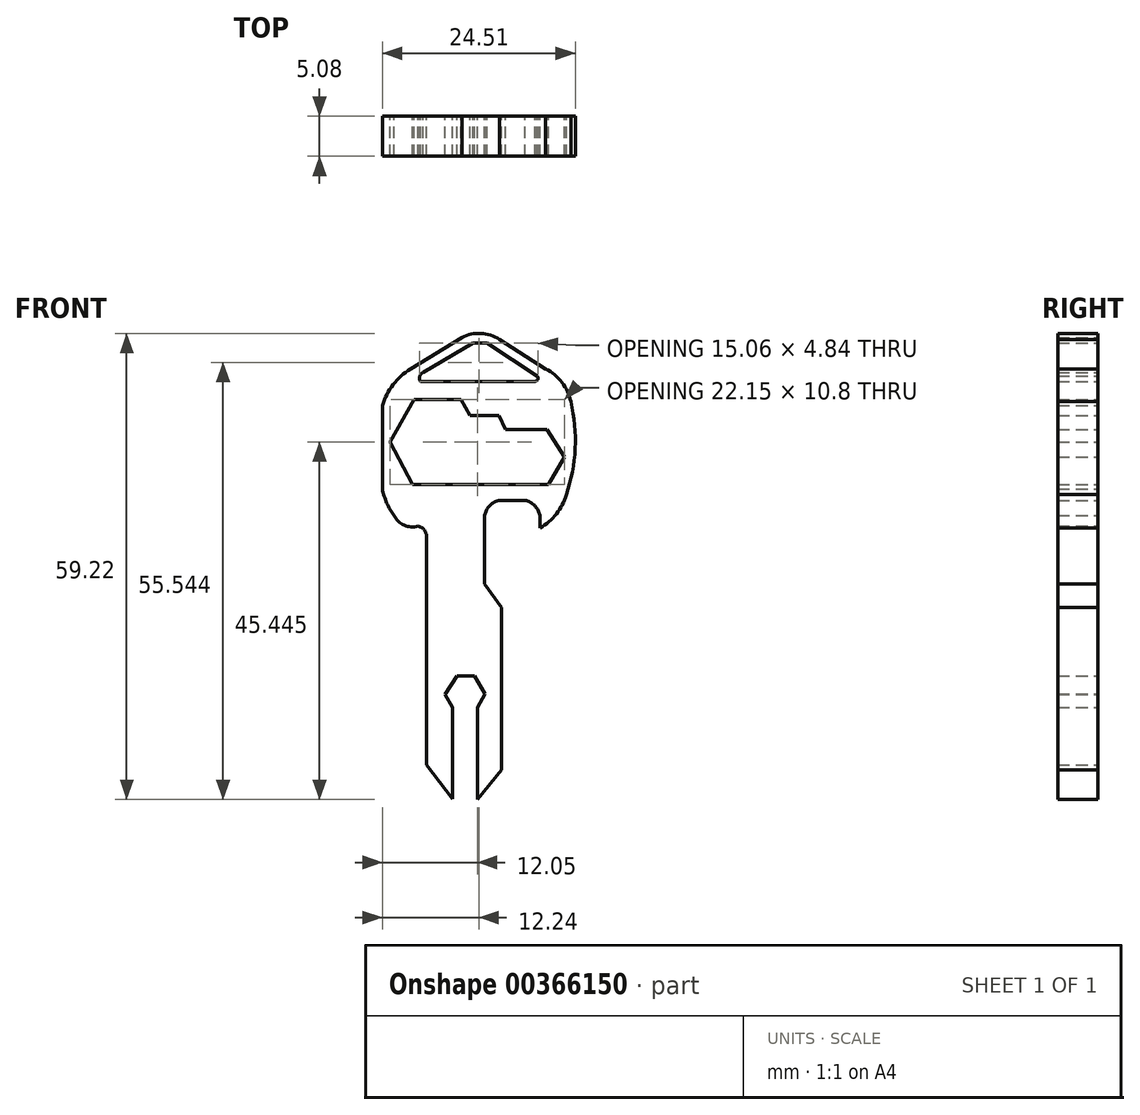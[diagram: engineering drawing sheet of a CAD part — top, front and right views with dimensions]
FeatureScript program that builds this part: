
annotation { "Feature Type Name" : "Feature", "Feature Type Description" : "" }
export const myFeature = defineFeature(function(context is Context, id is Id, definition is map)
    precondition{}
    {
        {
            var Q0;
            Q0=qCreatedBy(makeId("Front.planeOp"),FACE);
            var sketch = newSketch(context, id + "F0", { "sketchPlane" : qUnion([Q0])});
            skLineSegment(sketch, "E0", {"start": v(-17.2, 34.9) * mm, "end": v(6.42, 34.9) * mm});
            skLineSegment(sketch, "E1", {"start": v(-23.37, 27.1) * mm, "end": v(-23.37, -28.78) * mm});
            skLineSegment(sketch, "E2", {"start": v(-13.19, 21.69) * mm, "end": v(-7.23, 21.69) * mm});
            skLineSegment(sketch, "E3", {"start": v(-7.23, 21.69) * mm, "end": v(-6.06, 19.63) * mm});
            skLineSegment(sketch, "E4", {"start": v(-6.06, 19.63) * mm, "end": v(-2.36, 19.63) * mm});
            skLineSegment(sketch, "E5", {"start": v(-2.36, 19.63) * mm, "end": v(-1.54, 17.85) * mm});
            skLineSegment(sketch, "E6", {"start": v(-1.54, 17.85) * mm, "end": v(3.73, 17.85) * mm});
            skLineSegment(sketch, "E7", {"start": v(3.73, 17.85) * mm, "end": v(5.92, 14.34) * mm});
            skLineSegment(sketch, "E8", {"start": v(5.92, 14.34) * mm, "end": v(3.9, 10.88) * mm});
            skLineSegment(sketch, "E9", {"start": v(3.9, 10.88) * mm, "end": v(-13.37, 10.88) * mm});
            skLineSegment(sketch, "E10", {"start": v(-13.37, 10.88) * mm, "end": v(-16.22, 16.26) * mm});
            skLineSegment(sketch, "E11", {"start": v(-16.22, 16.26) * mm, "end": v(-13.19, 21.69) * mm});
            skLineSegment(sketch, "E12", {"start": v(2.2, 23.96) * mm, "end": v(-12.39, 23.96) * mm});
            skArc(sketch, "E13", {"start": v(2.2, 23.96) * mm, "mid": v(2.55, 24.24) * mm, "end": v(2.44, 24.67) * mm});
            skLineSegment(sketch, "E14", {"start": v(2.44, 24.67) * mm, "end": v(-3.92, 28.8) * mm});
            skLineSegment(sketch, "E15", {"start": v(-3.92, 28.8) * mm, "end": v(-5.67, 28.8) * mm});
            skLineSegment(sketch, "E16", {"start": v(-5.67, 28.8) * mm, "end": v(-12.04, 25.1) * mm});
            skArc(sketch, "E17", {"start": v(-12.04, 25.1) * mm, "mid": v(-12.46, 24.6) * mm, "end": v(-12.39, 23.96) * mm});
            skLineSegment(sketch, "E18", {"start": v(-11.57, 4.2) * mm, "end": v(-11.57, -24.78) * mm});
            skLineSegment(sketch, "E19", {"start": v(-11.57, -24.78) * mm, "end": v(-8.28, -29.1) * mm});
            skLineSegment(sketch, "E20", {"start": v(-8.28, -29.1) * mm, "end": v(-8.28, -17.45) * mm});
            skLineSegment(sketch, "E21", {"start": v(-8.28, -17.45) * mm, "end": v(-9.24, -15.83) * mm});
            skLineSegment(sketch, "E22", {"start": v(-9.24, -15.83) * mm, "end": v(-7.73, -13.46) * mm});
            skLineSegment(sketch, "E23", {"start": v(-7.73, -13.46) * mm, "end": v(-5.5, -13.46) * mm});
            skLineSegment(sketch, "E24", {"start": v(-5.5, -13.46) * mm, "end": v(-4.15, -15.72) * mm});
            skLineSegment(sketch, "E25", {"start": v(-4.15, -15.72) * mm, "end": v(-5.12, -17.45) * mm});
            skLineSegment(sketch, "E26", {"start": v(-5.12, -17.45) * mm, "end": v(-5.12, -29.16) * mm});
            skLineSegment(sketch, "E27", {"start": v(-5.12, -29.16) * mm, "end": v(-2.07, -25.4) * mm});
            skLineSegment(sketch, "E28", {"start": v(-2.07, -25.4) * mm, "end": v(-2.07, -4.78) * mm});
            skLineSegment(sketch, "E29", {"start": v(-2.07, -4.78) * mm, "end": v(-4.22, -1.79) * mm});
            skLineSegment(sketch, "E30", {"start": v(-4.22, -1.79) * mm, "end": v(-4.22, 6.9) * mm});
            skLineSegment(sketch, "E31", {"start": v(-2.28, 8.84) * mm, "end": v(0.9, 8.84) * mm});
            skLineSegment(sketch, "E32", {"start": v(2.82, 6.9) * mm, "end": v(2.82, 5.36) * mm});
            skArc(sketch, "E33", {"start": v(-2.33, 29.27) * mm, "mid": v(-4.69, 30.05) * mm, "end": v(-7.12, 29.53) * mm});
            skArc(sketch, "E34", {"start": v(6.73, 21.37) * mm, "mid": v(5.61, 23.82) * mm, "end": v(3.54, 25.55) * mm});
            skLineSegment(sketch, "E35", {"start": v(3.54, 25.55) * mm, "end": v(-2.33, 29.27) * mm});
            skArc(sketch, "E36", {"start": v(6.15, 9.56) * mm, "mid": v(7.28, 15.43) * mm, "end": v(6.73, 21.37) * mm});
            skArc(sketch, "E37", {"start": v(2.82, 5.36) * mm, "mid": v(4.9, 7.14) * mm, "end": v(6.15, 9.56) * mm});
            skLineSegment(sketch, "E38", {"start": v(-7.12, 29.53) * mm, "end": v(-13.65, 25.53) * mm});
            skArc(sketch, "E39", {"start": v(-13.65, 25.53) * mm, "mid": v(-15.85, 23.55) * mm, "end": v(-17.2, 20.93) * mm});
            skLineSegment(sketch, "E40", {"start": v(-17.2, 20.93) * mm, "end": v(-17.2, 10.27) * mm});
            skArc(sketch, "E41", {"start": v(-11.57, 4.2) * mm, "mid": v(-11.87, 5.07) * mm, "end": v(-12.66, 5.57) * mm});
            skArc(sketch, "E42", {"start": v(-15.74, 6.9) * mm, "mid": v(-14.43, 5.7) * mm, "end": v(-12.66, 5.57) * mm});
            skArc(sketch, "E43", {"start": v(-17.2, 10.27) * mm, "mid": v(-16.65, 8.51) * mm, "end": v(-15.74, 6.9) * mm});
            skArc(sketch, "E44", {"start": v(-2.28, 8.84) * mm, "mid": v(-3.56, 8.18) * mm, "end": v(-4.22, 6.9) * mm});
            skArc(sketch, "E45", {"start": v(2.82, 6.9) * mm, "mid": v(2.15, 8.17) * mm, "end": v(0.9, 8.84) * mm});
            skSolve(sketch);
        }
        {
            var Q0;
            Q0 = qSketchRegion(id + "F0", true);
            extrude(context, id + "F1", {"entities" : qUnion([Q0]), "depth" : 5.08 * mm, "offsetDistance" : 25.4 * mm});
        }
    });
